# Revit family: Wye_Pattern_Strainers-Backflow_Preventor-WATTS-77F-CSSI
name_source: partatom
category: Pipe Accessories
revit_build: Autodesk Revit 2014 (Build: 20130308_1515(x64)
units: mm (PartAtom-declared; Revit-internal decimal feet)

## types (9) — shared parameters
Assembly Code = F1050
CW Connection = Yes
Country = United States
Description = Stainless Steel, Flanged, Wye-Pattern Strainers
Finish = Metal-Watts-Stainless Steel
HW Connection = No
Manufacturer = WATTS
Manufacturer Product Line = Strainers
Material = Metal-Watts-Stainless Steel
Max. Working Pressure = 275psi (19.0 bar) at 100°F (38°C) WOG  150psi (10.3 bar) at 400°F (204°C) WSP
Model = 77F-CSI
Price = Prices may vary. Please consult Manufacturer Representative for most up-to-date price list.
Product Documentation Link = http://media.wattswater.com
Product Page URL = http://www.watts.com
Region = North America
URL = http://www.watts.com
Vent Connection = No
Warranty Information = 1 Year Limited Warranty
Waste Connection = No

## per-type parameters (varying)
| type | A | B | Body Radius | Connection Inlet Description | Connection Outlet Description | Connection Radius | Connection Size | Flange Thickness | NPT Diameter | NPT Radius | Nominal Depth | Nominal Depth 2 | Strainer Diameter | Strainer Length | Strainer Offset Length From Flange | Strainer Revolve Offset Distance | Strainer Thickness | Strainer Width | Weight | Width |
| 77F-CSSI 2" | 8 5/8" | 5 1/4" | 1 1/4" | 2" NPT Flanged Inlet | 2" NPT Flanged Outlet | 1" | 2" | 3/8" | 1/2" | 1/4" | 1" | 1/2" | 2 1/2" | 3 7/8" | 11/16" | 1 15/16" | 3/4" | 3 7/8" | 20/9.0 (LB/KG) | 4 1/4" |
| 77F-CSSI 2.5" | 10 1/4" | 7 1/2" | 1 5/8" | 2-1/2" NPT Flanged Inlet | 2-1/2" NPT Flanged Outlet | 1 1/4" | 2 1/2" | 3/8" | 3/4" | 3/8" | 1" | 1/2" | 2 3/4" | 4 7/8" | 1 1/16" | 2 7/16" | 3/4" | 4 7/8" | 32/14.5 (LB/KG) | 5" |
| 77F-CSSI 3" | 11 5/8" | 7" | 2" | 3" NPT Flanged Inlet | 3" NPT Flanged Outlet | 1 1/2" | 3" | 1/2" | 1" | 1/2" | 1 3/8" | 11/16" | 3 3/4" | 5" | 5/8" | 2 1/2" | 1" | 5" | 36/16.3 (LB/KG) | 5 1/2" |
| 77F-CSSI 4" | 14 3/8" | 9 1/8" | 2 1/2" | 4" NPT Flanged Inlet | 4" NPT Flanged Outlet | 2" | 4" | 1/2" | 1 1/2" | 3/4" | 1 5/8" | 13/16" | 4 3/4" | 6 1/8" | 11/16" | 3 1/16" | 1" | 6 1/8" | 61/27.6 (LB/KG) | 7" |
| 77F-CSSI 6" | 18 5/8" | 13" | 3 1/2" | 6" NPT Flanged Inlet | 6" NPT Flanged Outlet | 3" | 6" | 1" | 2" | 1" | 2 1/2" | 1 1/4" | 7" | 8 1/2" | 3/4" | 4 1/4" | 2" | 8 1/2" | 160/72.5 (LB/KG) | 10" |
| 77F-CSSI 0.75" | 7" | 4 1/4" | 1" | 3/4" NPT Flanged Inlet | 3/4" NPT Flanged Outlet | 3/8" | 3/4" | 1/4" | 3/8" | 3/16" | 5/8" | 5/16" | 1 5/8" | 2 7/8" | 5/8" | 1 7/16" | 7/16" | 2 7/8" | 7/2.9 (LB/KG) | 3" |
| 77F-CSSI 1" | 7 1/2" | 4 3/4" | 1" | 1" NPT Flanged Inlet | 1" NPT Flanged Outlet | 1/2" | 1" | 1/4" | 1/2" | 1/4" | 5/8" | 5/16" | 1 3/4" | 2 7/8" | 9/16" | 1 7/16" | 7/16" | 2 7/8" | 9/4.0 (LB/KG) | 3" |
| 77F-CSSI 1.5" | 9" | 5 5/8" | 1" | 1-1/2" NPT Flanged Inlet | 1-1/2" NPT Flanged Outlet | 3/4" | 1 1/2" | 1/4" | 1/2" | 1/4" | 3/4" | 3/8" | 2" | 3 1/2" | 3/4" | 1 3/4" | 7/16" | 3 1/2" | 12/5.4 (LB/KG) | 3 5/8" |
| 77F-CSSI 0.5" | 6" | 3 7/8" | 1" | 1/2" NPT Flanged Inlet | 1/2" NPT Flanged Outlet | 1/4" | 1/2" | 1/4" | 1/4" | 1/8" | 5/8" | 5/16" | 1 1/2" | 2 7/8" | 11/16" | 1 7/16" | 7/16" | 2 7/8" | 6/2.4 (LB/KG) | 3" |

## geometry (parser evidence)
native form markers: Revolve x1, Sweep x1
no freeform markers — native parametric forms only
